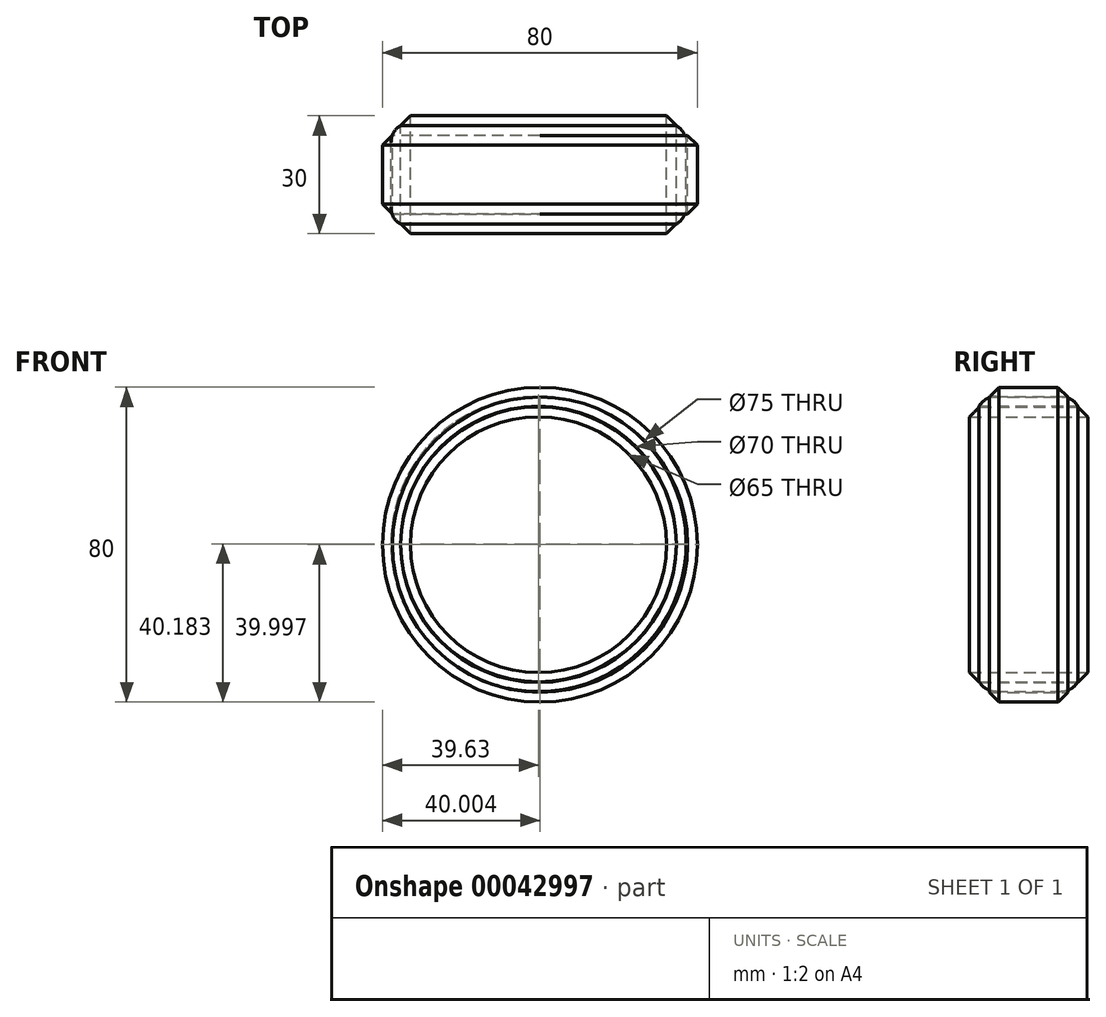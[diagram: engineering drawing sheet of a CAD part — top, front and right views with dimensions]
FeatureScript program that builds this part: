
annotation { "Feature Type Name" : "Feature", "Feature Type Description" : "" }
export const myFeature = defineFeature(function(context is Context, id is Id, definition is map)
    precondition{}
    {
        {
            var Q0;
            Q0=qCreatedBy(makeId("Front.planeOp"),FACE);
            var sketch = newSketch(context, id + "F0", { "sketchPlane" : qUnion([Q0])});
            skCircle(sketch, "E0", {"center": v(-3.18, -0.1) * mm, "radius": 40 * mm});
            skCircle(sketch, "E1", {"center": v(-3.18, -0.1) * mm, "radius": 37.5 * mm});
            skSolve(sketch);
        }
        {
            var Q0;
            Q0=qCreatedBy(makeId("Front.planeOp"),FACE);
            var sketch = newSketch(context, id + "F1", { "sketchPlane" : qUnion([Q0])});
            skCircle(sketch, "E2", {"center": v(-3.55, -0.1) * mm, "radius": 35 * mm});
            skCircle(sketch, "E3", {"center": v(-3.55, -0.1) * mm, "radius": 32.5 * mm});
            skSolve(sketch);
        }
        {
            var Q0;
            Q0=qCreatedBy(makeId("Front.planeOp"),FACE);
            var sketch = newSketch(context, id + "F2", { "sketchPlane" : qUnion([Q0])});
            skCircle(sketch, "E4", {"center": v(-3.55, 0.1) * mm, "radius": 35 * mm});
            skCircle(sketch, "E5", {"center": v(-3.55, 0.1) * mm, "radius": 37.5 * mm});
            skSolve(sketch);
        }
        {
            var Q0;
            Q0 = qSketchRegion(id + "F1", true);
            extrude(context, id + "F3", {"entities" : qUnion([Q0]), "depth" : 30 * mm, "hasSecondDirection" : true, "secondDirectionOppositeDirection" : true, "secondDirectionDepth" : 5 * mm});
        }
        {
            var Q0;
            Q0 = qSketchRegion(id + "F0", true);
            extrude(context, id + "F4", {"entities" : qUnion([Q0]), "depth" : 25 * mm});
        }
        {
            var Q0;
            Q0=makeQuery(id+"F4.opExtrude","SWEPT_FACE",FACE,{"disambiguationData":[OSD([sQuery(id+"F0.wireOp",EDGE,"E0")])]});
            var Q1;
            Q1=makeQuery(id+"F3.opExtrude","SWEPT_FACE",FACE,{"disambiguationData":[OSD([sQuery(id+"F1.wireOp",EDGE,"E2")])]});
            chamfer(context, id + "F5", {"entities" : qUnion([Q0, Q1]), "width" : 5 * mm, "tangentPropagation" : true});
        }
        {
            var Q0;
            Q0 = qSketchRegion(id + "F2", true);
            var Q1;
            {var subQ0=sQuery(id+"F1.wireOp",EDGE,"E2");Q1=makeQuery(id+"F5.opChamfer","BLEND_FACE",FACE,{"disambiguationData":[OSD([subQ0]),TDD([makeQuery(id+"F3.opExtrude","CAP_EDGE",EDGE,{"disambiguationData":[OSD([subQ0])],"isStart":false})])]});}
            extrude(context, id + "F6", {"entities" : qUnion([Q0]), "endBoundEntityFace" : qUnion([Q1]), "depth" : 25.07 * mm});
        }
        {
            var Q0;
            Q0=makeQuery(id+"F6.opExtrude","CAP_EDGE",EDGE,{"disambiguationData":[OSD([sQuery(id+"F2.wireOp",EDGE,"E5")])],"isStart":false});
            var Q1;
            Q1=makeQuery(id+"F6.opExtrude","CAP_EDGE",EDGE,{"disambiguationData":[OSD([sQuery(id+"F2.wireOp",EDGE,"E5")])],"isStart":true});
            fillet(context, id + "F7", {"entities" : qUnion([Q0, Q1]), "radius" : 5 * mm, "tangentPropagation" : true, "allowEdgeOverflow" : false});
        }
    });
